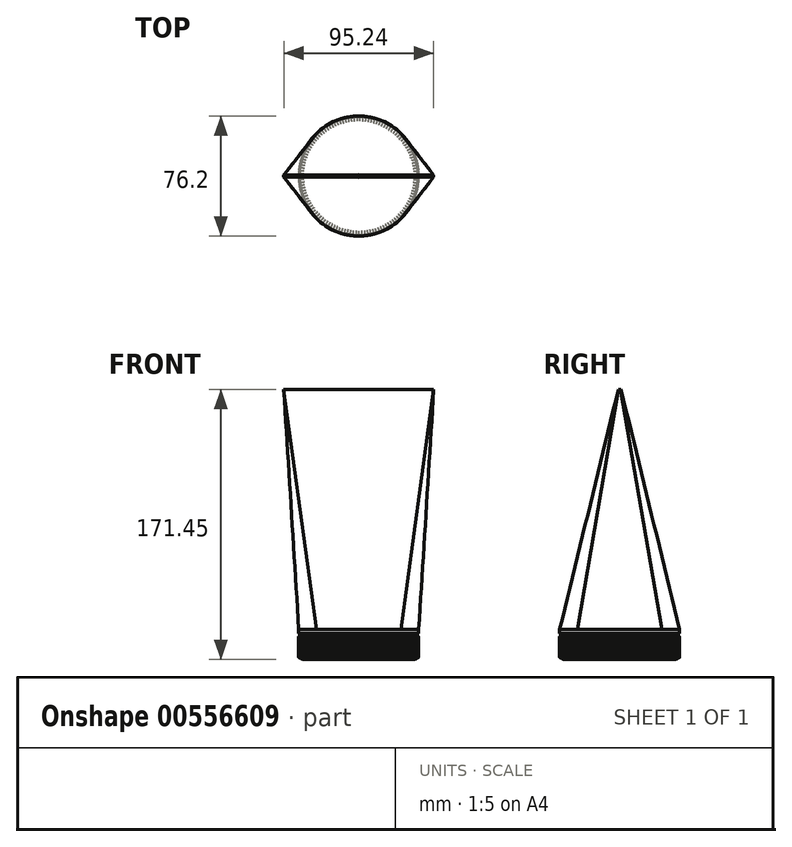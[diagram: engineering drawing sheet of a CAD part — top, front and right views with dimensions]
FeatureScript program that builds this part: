
annotation { "Feature Type Name" : "Feature", "Feature Type Description" : "" }
export const myFeature = defineFeature(function(context is Context, id is Id, definition is map)
    precondition{}
    {
        {
            var Q0;
            Q0=qCreatedBy(makeId("Top.planeOp"),FACE);
            var sketch = newSketch(context, id + "F0", { "sketchPlane" : qUnion([Q0])});
            skCircle(sketch, "E0", {"center": v(0, 0) * mm, "radius": 38.1 * mm});
            skSolve(sketch);
        }
        {
            var Q0;
            Q0=qCreatedBy(makeId("Top.planeOp"),FACE);
            cPlane(context, id + "F1", {"entities" : qUnion([Q0]), "cplaneType" : CPlaneType.OFFSET, "offset" : 152.4 * mm, "width" : 152.4 * mm, "height" : 152.4 * mm});
        }
        {
            var Q0;
            Q0=qCreatedBy(id+"F1.planeOp",FACE);
            var sketch = newSketch(context, id + "F2", { "sketchPlane" : qUnion([Q0])});
            skLineSegment(sketch, "E1", {"start": v(-47.63, 0) * mm, "end": v(47.63, 0) * mm, "construction": true});
            skLineSegment(sketch, "E2", {"start": v(-47.63, 0) * mm, "end": v(-47.63, 0.64) * mm});
            skLineSegment(sketch, "E3", {"start": v(-47.63, 0.64) * mm, "end": v(0, 0.89) * mm});
            skLineSegment(sketch, "E4", {"start": v(0, 0.89) * mm, "end": v(47.63, 0.64) * mm});
            skLineSegment(sketch, "E5", {"start": v(47.63, 0.64) * mm, "end": v(47.63, 0) * mm});
            skLineSegment(sketch, "E6.MirrorCS", {"start": v(47.63, -0.64) * mm, "end": v(47.63, 0) * mm});
            skLineSegment(sketch, "E7.MirrorCS", {"start": v(-47.63, 0) * mm, "end": v(-47.63, -0.64) * mm});
            skLineSegment(sketch, "E8.MirrorCS", {"start": v(-47.63, -0.64) * mm, "end": v(0, -0.89) * mm});
            skLineSegment(sketch, "E9.MirrorCS", {"start": v(0, -0.89) * mm, "end": v(47.63, -0.64) * mm});
            skSolve(sketch);
        }
        {
            var Q0;
            Q0=makeQuery(id+"F0.imprint","IMPRINT",FACE,{"disambiguationData":[TD([[makeQuery(id+"F0.imprint","IMPRINT",EDGE,{"derivedFrom":sQuery(id+"F0.wireOp",EDGE,"E0")}),1.0]])]});
            var Q1;
            Q1=makeQuery(id+"F2.imprint","IMPRINT",FACE,{"disambiguationData":[TD([[makeQuery(id+"F2.imprint","IMPRINT",EDGE,{"derivedFrom":sQuery(id+"F2.wireOp",EDGE,"E2")}),-1.0]])]});
            loft(context, id + "F3", {"sheetProfilesArray" : [{ "sheetProfileEntities" : qUnion([Q0]) }, { "sheetProfileEntities" : qUnion([Q1]) }]});
        }
        {
            var Q0;
            Q0=qCreatedBy(makeId("Right.planeOp"),FACE);
            var sketch = newSketch(context, id + "F4", { "sketchPlane" : qUnion([Q0])});
            skLineSegment(sketch, "E10", {"start": v(0, 0) * mm, "end": v(0, -19.05) * mm});
            skLineSegment(sketch, "E11", {"start": v(0, -19.05) * mm, "end": v(38.1, -19.05) * mm});
            skLineSegment(sketch, "E12", {"start": v(38.1, -19.05) * mm, "end": v(38.1, -4.45) * mm});
            skLineSegment(sketch, "E13", {"start": v(38.1, -4.45) * mm, "end": v(37.46, -4.45) * mm});
            skLineSegment(sketch, "E14", {"start": v(37.46, -4.45) * mm, "end": v(37.46, -2.54) * mm});
            skLineSegment(sketch, "E15", {"start": v(37.46, -2.54) * mm, "end": v(38.1, -2.54) * mm});
            skLineSegment(sketch, "E16", {"start": v(38.1, -2.54) * mm, "end": v(38.1, 0) * mm});
            skLineSegment(sketch, "E17", {"start": v(38.1, 0) * mm, "end": v(0, 0) * mm});
            skSolve(sketch);
        }
        {
            var Q0;
            Q0 = qSketchRegion(id + "F4", true);
            var Q1;
            Q1=sQuery(id+"F4.wireOp",EDGE,"E10");
            revolve(context, id + "F5", {"entities" : qUnion([Q0]), "axis" : qUnion([Q1]), "revolveType" : RevolveType.FULL});
        }
        {
            var Q0;
            Q0=makeQuery(id+"F5.opRevolve","SWEPT_FACE",FACE,{"disambiguationData":[OSD([sQuery(id+"F4.wireOp",EDGE,"E13")])]});
            var sketch = newSketch(context, id + "F6", { "sketchPlane" : qUnion([Q0])});
            skCircle(sketch, "E18", {"center": v(0, 38.1) * mm, "radius": 0.64 * mm});
            skCircle(sketch, "E19.1.0", {"center": v(-1.91, 38.05) * mm, "radius": 0.64 * mm});
            skCircle(sketch, "E19.2.0", {"center": v(-3.82, 37.9) * mm, "radius": 0.64 * mm});
            skCircle(sketch, "E19.3.0", {"center": v(-5.72, 37.67) * mm, "radius": 0.64 * mm});
            skCircle(sketch, "E19.4.0", {"center": v(-7.6, 37.33) * mm, "radius": 0.64 * mm});
            skCircle(sketch, "E19.5.0", {"center": v(-9.48, 36.9) * mm, "radius": 0.64 * mm});
            skCircle(sketch, "E19.6.0", {"center": v(-11.32, 36.38) * mm, "radius": 0.64 * mm});
            skCircle(sketch, "E19.7.0", {"center": v(-13.13, 35.77) * mm, "radius": 0.64 * mm});
            skCircle(sketch, "E19.8.0", {"center": v(-14.91, 35.06) * mm, "radius": 0.64 * mm});
            skCircle(sketch, "E19.9.0", {"center": v(-16.65, 34.27) * mm, "radius": 0.64 * mm});
            skCircle(sketch, "E19.10.0", {"center": v(-18.35, 33.39) * mm, "radius": 0.64 * mm});
            skCircle(sketch, "E19.11.0", {"center": v(-20, 32.42) * mm, "radius": 0.64 * mm});
            skCircle(sketch, "E19.12.0", {"center": v(-21.61, 31.38) * mm, "radius": 0.64 * mm});
            skCircle(sketch, "E19.13.0", {"center": v(-23.16, 30.25) * mm, "radius": 0.64 * mm});
            skCircle(sketch, "E19.14.0", {"center": v(-24.65, 29.05) * mm, "radius": 0.64 * mm});
            skCircle(sketch, "E19.15.0", {"center": v(-26.08, 27.77) * mm, "radius": 0.64 * mm});
            skCircle(sketch, "E19.16.0", {"center": v(-27.44, 26.43) * mm, "radius": 0.64 * mm});
            skCircle(sketch, "E19.17.0", {"center": v(-28.74, 25.02) * mm, "radius": 0.64 * mm});
            skCircle(sketch, "E19.18.0", {"center": v(-29.96, 23.54) * mm, "radius": 0.64 * mm});
            skCircle(sketch, "E19.19.0", {"center": v(-31.1, 22) * mm, "radius": 0.64 * mm});
            skCircle(sketch, "E19.20.0", {"center": v(-32.17, 20.42) * mm, "radius": 0.64 * mm});
            skCircle(sketch, "E19.21.0", {"center": v(-33.15, 18.77) * mm, "radius": 0.64 * mm});
            skCircle(sketch, "E19.22.0", {"center": v(-34.06, 17.08) * mm, "radius": 0.64 * mm});
            skCircle(sketch, "E19.23.0", {"center": v(-34.87, 15.35) * mm, "radius": 0.64 * mm});
            skCircle(sketch, "E19.24.0", {"center": v(-35.6, 13.58) * mm, "radius": 0.64 * mm});
            skCircle(sketch, "E19.25.0", {"center": v(-36.24, 11.77) * mm, "radius": 0.64 * mm});
            skCircle(sketch, "E19.26.0", {"center": v(-36.78, 9.94) * mm, "radius": 0.64 * mm});
            skCircle(sketch, "E19.27.0", {"center": v(-37.23, 8.08) * mm, "radius": 0.64 * mm});
            skCircle(sketch, "E19.28.0", {"center": v(-37.6, 6.2) * mm, "radius": 0.64 * mm});
            skCircle(sketch, "E19.29.0", {"center": v(-37.86, 4.3) * mm, "radius": 0.64 * mm});
            skCircle(sketch, "E19.30.0", {"center": v(-38.02, 2.4) * mm, "radius": 0.64 * mm});
            skCircle(sketch, "E19.31.0", {"center": v(-38.1, 0.48) * mm, "radius": 0.64 * mm});
            skCircle(sketch, "E19.32.0", {"center": v(-38.07, -1.44) * mm, "radius": 0.64 * mm});
            skCircle(sketch, "E19.33.0", {"center": v(-37.95, -3.35) * mm, "radius": 0.64 * mm});
            skCircle(sketch, "E19.34.0", {"center": v(-37.74, -5.25) * mm, "radius": 0.64 * mm});
            skCircle(sketch, "E19.35.0", {"center": v(-37.43, -7.14) * mm, "radius": 0.64 * mm});
            skCircle(sketch, "E19.36.0", {"center": v(-37.02, -9.01) * mm, "radius": 0.64 * mm});
            skCircle(sketch, "E19.37.0", {"center": v(-36.52, -10.86) * mm, "radius": 0.64 * mm});
            skCircle(sketch, "E19.38.0", {"center": v(-35.93, -12.68) * mm, "radius": 0.64 * mm});
            skCircle(sketch, "E19.39.0", {"center": v(-35.25, -14.47) * mm, "radius": 0.64 * mm});
            skCircle(sketch, "E19.40.0", {"center": v(-34.47, -16.22) * mm, "radius": 0.64 * mm});
            skCircle(sketch, "E19.41.0", {"center": v(-33.62, -17.93) * mm, "radius": 0.64 * mm});
            skCircle(sketch, "E19.42.0", {"center": v(-32.67, -19.6) * mm, "radius": 0.64 * mm});
            skCircle(sketch, "E19.43.0", {"center": v(-31.65, -21.22) * mm, "radius": 0.64 * mm});
            skCircle(sketch, "E19.44.0", {"center": v(-30.54, -22.78) * mm, "radius": 0.64 * mm});
            skCircle(sketch, "E19.45.0", {"center": v(-29.36, -24.29) * mm, "radius": 0.64 * mm});
            skCircle(sketch, "E19.46.0", {"center": v(-28.1, -25.73) * mm, "radius": 0.64 * mm});
            skCircle(sketch, "E19.47.0", {"center": v(-26.77, -27.1) * mm, "radius": 0.64 * mm});
            skCircle(sketch, "E19.48.0", {"center": v(-25.38, -28.42) * mm, "radius": 0.64 * mm});
            skCircle(sketch, "E19.49.0", {"center": v(-23.92, -29.66) * mm, "radius": 0.64 * mm});
            skCircle(sketch, "E19.50.0", {"center": v(-22.4, -30.82) * mm, "radius": 0.64 * mm});
            skCircle(sketch, "E19.51.0", {"center": v(-20.82, -31.9) * mm, "radius": 0.64 * mm});
            skCircle(sketch, "E19.52.0", {"center": v(-19.19, -32.92) * mm, "radius": 0.64 * mm});
            skCircle(sketch, "E19.53.0", {"center": v(-17.5, -33.84) * mm, "radius": 0.64 * mm});
            skCircle(sketch, "E19.54.0", {"center": v(-15.79, -34.68) * mm, "radius": 0.64 * mm});
            skCircle(sketch, "E19.55.0", {"center": v(-14.03, -35.42) * mm, "radius": 0.64 * mm});
            skCircle(sketch, "E19.56.0", {"center": v(-12.23, -36.08) * mm, "radius": 0.64 * mm});
            skCircle(sketch, "E19.57.0", {"center": v(-10.4, -36.65) * mm, "radius": 0.64 * mm});
            skCircle(sketch, "E19.58.0", {"center": v(-8.54, -37.13) * mm, "radius": 0.64 * mm});
            skCircle(sketch, "E19.59.0", {"center": v(-6.67, -37.51) * mm, "radius": 0.64 * mm});
            skCircle(sketch, "E19.60.0", {"center": v(-4.78, -37.8) * mm, "radius": 0.64 * mm});
            skCircle(sketch, "E19.61.0", {"center": v(-2.87, -38) * mm, "radius": 0.64 * mm});
            skCircle(sketch, "E19.62.0", {"center": v(-0.96, -38.09) * mm, "radius": 0.64 * mm});
            skCircle(sketch, "E19.63.0", {"center": v(0.96, -38.09) * mm, "radius": 0.64 * mm});
            skCircle(sketch, "E19.64.0", {"center": v(2.87, -38) * mm, "radius": 0.64 * mm});
            skCircle(sketch, "E19.65.0", {"center": v(4.78, -37.8) * mm, "radius": 0.64 * mm});
            skCircle(sketch, "E19.66.0", {"center": v(6.67, -37.51) * mm, "radius": 0.64 * mm});
            skCircle(sketch, "E19.67.0", {"center": v(8.54, -37.13) * mm, "radius": 0.64 * mm});
            skCircle(sketch, "E19.68.0", {"center": v(10.4, -36.65) * mm, "radius": 0.64 * mm});
            skCircle(sketch, "E19.69.0", {"center": v(12.23, -36.08) * mm, "radius": 0.64 * mm});
            skCircle(sketch, "E19.70.0", {"center": v(14.03, -35.42) * mm, "radius": 0.64 * mm});
            skCircle(sketch, "E19.71.0", {"center": v(15.79, -34.68) * mm, "radius": 0.64 * mm});
            skCircle(sketch, "E19.72.0", {"center": v(17.5, -33.84) * mm, "radius": 0.64 * mm});
            skCircle(sketch, "E19.73.0", {"center": v(19.19, -32.92) * mm, "radius": 0.64 * mm});
            skCircle(sketch, "E19.74.0", {"center": v(20.82, -31.9) * mm, "radius": 0.64 * mm});
            skCircle(sketch, "E19.75.0", {"center": v(22.4, -30.82) * mm, "radius": 0.64 * mm});
            skCircle(sketch, "E19.76.0", {"center": v(23.92, -29.66) * mm, "radius": 0.64 * mm});
            skCircle(sketch, "E19.77.0", {"center": v(25.38, -28.42) * mm, "radius": 0.64 * mm});
            skCircle(sketch, "E19.78.0", {"center": v(26.77, -27.1) * mm, "radius": 0.64 * mm});
            skCircle(sketch, "E19.79.0", {"center": v(28.1, -25.73) * mm, "radius": 0.64 * mm});
            skCircle(sketch, "E19.80.0", {"center": v(29.36, -24.29) * mm, "radius": 0.64 * mm});
            skCircle(sketch, "E19.81.0", {"center": v(30.54, -22.78) * mm, "radius": 0.64 * mm});
            skCircle(sketch, "E19.82.0", {"center": v(31.65, -21.22) * mm, "radius": 0.64 * mm});
            skCircle(sketch, "E19.83.0", {"center": v(32.67, -19.6) * mm, "radius": 0.64 * mm});
            skCircle(sketch, "E19.84.0", {"center": v(33.62, -17.93) * mm, "radius": 0.64 * mm});
            skCircle(sketch, "E19.85.0", {"center": v(34.47, -16.22) * mm, "radius": 0.64 * mm});
            skCircle(sketch, "E19.86.0", {"center": v(35.25, -14.47) * mm, "radius": 0.64 * mm});
            skCircle(sketch, "E19.87.0", {"center": v(35.93, -12.68) * mm, "radius": 0.64 * mm});
            skCircle(sketch, "E19.88.0", {"center": v(36.52, -10.86) * mm, "radius": 0.64 * mm});
            skCircle(sketch, "E19.89.0", {"center": v(37.02, -9.01) * mm, "radius": 0.64 * mm});
            skCircle(sketch, "E19.90.0", {"center": v(37.43, -7.14) * mm, "radius": 0.64 * mm});
            skCircle(sketch, "E19.91.0", {"center": v(37.74, -5.25) * mm, "radius": 0.64 * mm});
            skCircle(sketch, "E19.92.0", {"center": v(37.95, -3.35) * mm, "radius": 0.64 * mm});
            skCircle(sketch, "E19.93.0", {"center": v(38.07, -1.44) * mm, "radius": 0.64 * mm});
            skCircle(sketch, "E19.94.0", {"center": v(38.1, 0.48) * mm, "radius": 0.64 * mm});
            skCircle(sketch, "E19.95.0", {"center": v(38.02, 2.4) * mm, "radius": 0.64 * mm});
            skCircle(sketch, "E19.96.0", {"center": v(37.86, 4.3) * mm, "radius": 0.64 * mm});
            skCircle(sketch, "E19.97.0", {"center": v(37.6, 6.2) * mm, "radius": 0.64 * mm});
            skCircle(sketch, "E19.98.0", {"center": v(37.23, 8.08) * mm, "radius": 0.64 * mm});
            skCircle(sketch, "E19.99.0", {"center": v(36.78, 9.94) * mm, "radius": 0.64 * mm});
            skCircle(sketch, "E19.100.0", {"center": v(36.24, 11.77) * mm, "radius": 0.64 * mm});
            skCircle(sketch, "E19.101.0", {"center": v(35.6, 13.58) * mm, "radius": 0.64 * mm});
            skCircle(sketch, "E19.102.0", {"center": v(34.87, 15.35) * mm, "radius": 0.64 * mm});
            skCircle(sketch, "E19.103.0", {"center": v(34.06, 17.08) * mm, "radius": 0.64 * mm});
            skCircle(sketch, "E19.104.0", {"center": v(33.15, 18.77) * mm, "radius": 0.64 * mm});
            skCircle(sketch, "E19.105.0", {"center": v(32.17, 20.42) * mm, "radius": 0.64 * mm});
            skCircle(sketch, "E19.106.0", {"center": v(31.1, 22) * mm, "radius": 0.64 * mm});
            skCircle(sketch, "E19.107.0", {"center": v(29.96, 23.54) * mm, "radius": 0.64 * mm});
            skCircle(sketch, "E19.108.0", {"center": v(28.74, 25.02) * mm, "radius": 0.64 * mm});
            skCircle(sketch, "E19.109.0", {"center": v(27.44, 26.43) * mm, "radius": 0.64 * mm});
            skCircle(sketch, "E19.110.0", {"center": v(26.08, 27.77) * mm, "radius": 0.64 * mm});
            skCircle(sketch, "E19.111.0", {"center": v(24.65, 29.05) * mm, "radius": 0.64 * mm});
            skCircle(sketch, "E19.112.0", {"center": v(23.16, 30.25) * mm, "radius": 0.64 * mm});
            skCircle(sketch, "E19.113.0", {"center": v(21.61, 31.38) * mm, "radius": 0.64 * mm});
            skCircle(sketch, "E19.114.0", {"center": v(20, 32.42) * mm, "radius": 0.64 * mm});
            skCircle(sketch, "E19.115.0", {"center": v(18.35, 33.39) * mm, "radius": 0.64 * mm});
            skCircle(sketch, "E19.116.0", {"center": v(16.65, 34.27) * mm, "radius": 0.64 * mm});
            skCircle(sketch, "E19.117.0", {"center": v(14.91, 35.06) * mm, "radius": 0.64 * mm});
            skCircle(sketch, "E19.118.0", {"center": v(13.13, 35.77) * mm, "radius": 0.64 * mm});
            skCircle(sketch, "E19.119.0", {"center": v(11.32, 36.38) * mm, "radius": 0.64 * mm});
            skCircle(sketch, "E19.120.0", {"center": v(9.48, 36.9) * mm, "radius": 0.64 * mm});
            skCircle(sketch, "E19.121.0", {"center": v(7.6, 37.33) * mm, "radius": 0.64 * mm});
            skCircle(sketch, "E19.122.0", {"center": v(5.72, 37.67) * mm, "radius": 0.64 * mm});
            skCircle(sketch, "E19.123.0", {"center": v(3.82, 37.9) * mm, "radius": 0.64 * mm});
            skCircle(sketch, "E19.124.0", {"center": v(1.91, 38.05) * mm, "radius": 0.64 * mm});
            skPoint(sketch, "E19.center", {"position": v(0, 0) * mm});
            skSolve(sketch);
        }
        {
            var Q0;
            Q0 = qSketchRegion(id + "F6", true);
            extrude(context, id + "F7", {"entities" : qUnion([Q0]), "operationType" : NewBodyOperationType.REMOVE, "oppositeDirection" : true, "depth" : 14.6 * mm, "offsetDistance" : 25.4 * mm, "hasDraft" : true, "draftAngle" : 2 * degree, "draftPullDirection" : true});
        }
        {
            var Q0;
            Q0=makeQuery(id+"F5.opRevolve","SWEPT_FACE",FACE,{"disambiguationData":[OSD([sQuery(id+"F4.wireOp",EDGE,"E11")])]});
            fillet(context, id + "F8", {"entities" : qUnion([Q0]), "radius" : 3.17 * mm, "tangentPropagation" : true, "allowEdgeOverflow" : false});
        }
    });
